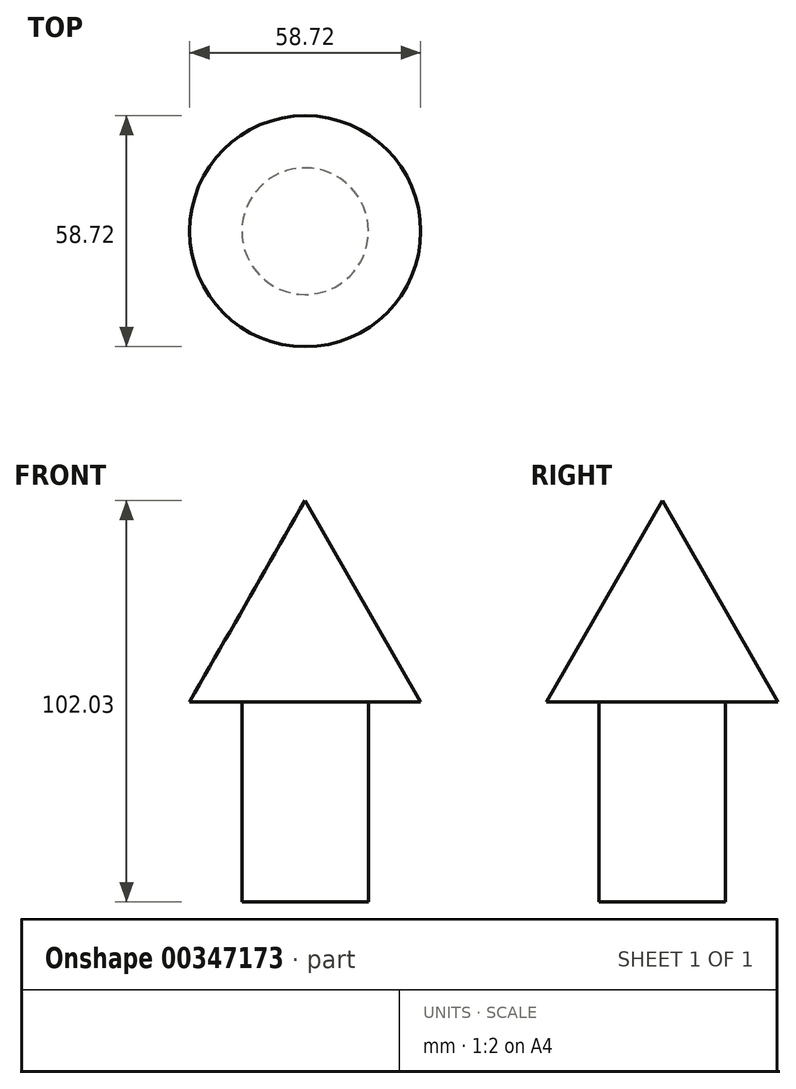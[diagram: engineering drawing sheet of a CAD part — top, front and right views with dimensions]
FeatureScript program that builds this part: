
annotation { "Feature Type Name" : "Feature", "Feature Type Description" : "" }
export const myFeature = defineFeature(function(context is Context, id is Id, definition is map)
    precondition{}
    {
        {
            var Q0;
            Q0=qCreatedBy(makeId("Front.planeOp"),FACE);
            var sketch = newSketch(context, id + "F0", { "sketchPlane" : qUnion([Q0])});
            skLineSegment(sketch, "E0", {"start": v(0, 38.28) * mm, "end": v(29.36, -12.95) * mm});
            skLineSegment(sketch, "E1", {"start": v(29.36, -12.95) * mm, "end": v(0, -12.95) * mm});
            skLineSegment(sketch, "E2", {"start": v(0, -12.95) * mm, "end": v(0, 38.28) * mm});
            skSolve(sketch);
        }
        {
            var Q0;
            Q0 = qSketchRegion(id + "F0", true);
            var Q1;
            Q1=sQuery(id+"F0.wireOp",EDGE,"E2");
            revolve(context, id + "F1", {"entities" : qUnion([Q0]), "axis" : qUnion([Q1]), "revolveType" : RevolveType.FULL});
        }
        {
            var Q0;
            Q0=makeQuery(id+"F1.opRevolve","SWEPT_FACE",FACE,{"disambiguationData":[OSD([sQuery(id+"F0.wireOp",EDGE,"E1")])]});
            var sketch = newSketch(context, id + "F2", { "sketchPlane" : qUnion([Q0])});
            skCircle(sketch, "E3", {"center": v(0, 0) * mm, "radius": 16.09 * mm});
            skSolve(sketch);
        }
        {
            var Q0;
            Q0 = qSketchRegion(id + "F2", true);
            var Q1;
            Q1=makeQuery(id+"F2.imprint","IMPRINT",FACE,{"disambiguationData":[TD([[makeQuery(id+"F2.imprint","IMPRINT",EDGE,{"derivedFrom":sQuery(id+"F2.wireOp",EDGE,"E3")}),1.0]])]});
            extrude(context, id + "F3", {"entities" : qUnion([Q0, Q1]), "operationType" : NewBodyOperationType.ADD, "depth" : 50.8 * mm});
        }
    });
